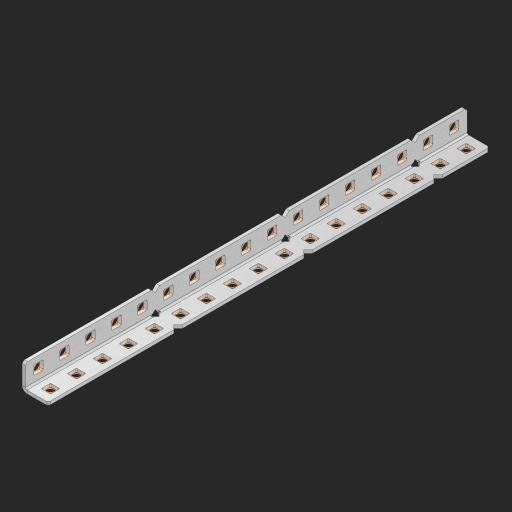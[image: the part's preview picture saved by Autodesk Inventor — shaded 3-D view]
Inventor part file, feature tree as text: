
AUTODESK INVENTOR PART (.ipt)
format: ipt  version: 2023 (Build 270158000, 158)  size: 751,616 bytes
history: native  units: in
note: dims shown in document units (in); Inventor stores cm internally (conversion verified against a paired STEP export)
features: other x40, extrude x35, sheet_metal_op x8, sketch x5, pattern_linear x1, mirror x1, chamfer x1
ambient origin geometry x8: Origin, YZ Plane, XZ Plane, XY Plane, X Axis, Y Axis, Z Axis, Center Point
bodies: Solid1 (feature_tree), Body (feature_tree)
feature tree (91):
  sheet_metal_op  "Flanges"
  sheet_metal_op  "Body Pattern"
  other  "Arc Length"
  pattern_linear  "Notch Pattern"  Spacing1=0.125in  [1 undecoded]
  other  "Diagonal Plane"
  mirror  "Everything Mirrored"
  chamfer  "End Chamfer"
  sketch  "Sketch1"  dims[d0=0.5in]
  other  "Plate1"
  sketch  "Sketch2"  dims[d1=8.5in]
  other  "Plate2"
  sheet_metal_op  "Bend1"
  sheet_metal_op  "Corner1"
  sketch  "Sketch8"  dims[d2=0.0625in]
  sketch  "Sketch9"  dims[d3=0.0625in]
  other  "Srf91"
  sheet_metal_op  "Body Pattern Sketch"
  other  "Srf92"
  sketch  "Sketch13"  dims[d4=0.0312in d5=0.125in d6=0.0625in d7=0.5in d8=90.0deg d9=0.0312in d10=0.25in d11=0.0625in d12=0.0625in d49=0.182in d50=0.02in d52=0.25in d53=0.0625in d54=0.0in d55=0.172in d56=1.0in d57=0.0in d85=0.1473in d86=0.1782in d89=0.0625in d90=0.0in d91=0.04in d92=0.0491in d95=2.5in d96=0.04in d97=0.25in d98=45.0deg d123=0.204in d126=0.0491in d127=0.1473in d128=0.08in d129=0.04in d130=2.5in d131=6.6929in d133=0.5in d134=0.3937in d136=1.0in]
  other  "Srf856"
  other  "Srf857"
  other  "Srf858"
  other  "Srf859"
  other  "Srf860"
  other  "Srf861"
  other  "Srf1275"
  other  "Srf1276"
  other  "Srf1278"
  other  "Srf1279"
  other  "Srf1280"
  other  "Srf1281"
  other  "Srf1282"
  other  "Srf1283"
  other  "Srf1383"
  other  "Srf1384"
  other  "Srf1385"
  other  "Srf1386"
  other  "Srf1387"
  other  "Srf1388"
  other  "Srf1389"
  other  "Srf1390"
  other  "Srf1391"
  other  "Srf1392"
  other  "Srf1475"
  other  "Srf1476"
  other  "Srf1477"
  other  "Srf1478"
  other  "Srf1479"
  other  "Srf1480"
  other  "Srf1481"
  other  "Srf1482"
  other  "Srf1483"
  other  "Srf1484"
  sheet_metal_op  "Body Stamp"
  sheet_metal_op  "Body Circle"
  sheet_metal_op  "Notch"
  extrude  "ExtrusionSrf92"  Depth=0.0625in
  extrude  "ExtrusionSrf856"  Depth=0.5in TaperAngle=90.0deg
  extrude  "ExtrusionSrf857"  Depth=0.25in
  extrude  "ExtrusionSrf858"  Depth=0.0625in
  extrude  "ExtrusionSrf859"  Depth=0.0625in
  extrude  "ExtrusionSrf860"  Depth=0.3937in
  extrude  "ExtrusionSrf861"  Depth=0.02in
  extrude  "ExtrusionSrf1275"  Depth=0.25in
  extrude  "ExtrusionSrf1276"  Depth=0.0625in
  extrude  "ExtrusionSrf1277"  TaperAngle=0.0deg  [1 undecoded]
  extrude  "ExtrusionSrf1278"  Depth=0.3937in
  extrude  "ExtrusionSrf1279"  Depth=0.3937in TaperAngle=0.0deg
  extrude  "ExtrusionSrf1280"  Depth=0.3937in
  extrude  "ExtrusionSrf1281"  Depth=0.3937in
  extrude  "ExtrusionSrf1282"  Depth=0.0625in
  extrude  "ExtrusionSrf1383"  Depth=0.3937in TaperAngle=0.0deg
  extrude  "ExtrusionSrf1384"  Depth=0.3937in
  extrude  "ExtrusionSrf1385"  Depth=0.25in TaperAngle=45.0deg
  extrude  "ExtrusionSrf1386"  Depth=0.3937in
  extrude  "ExtrusionSrf1387"  Depth=0.3937in
  extrude  "ExtrusionSrf1388"  Depth=0.3937in
  extrude  "ExtrusionSrf1389"  Depth=0.3937in
  extrude  "ExtrusionSrf1390"  Depth=0.3937in
  extrude  "ExtrusionSrf1391"  Depth=0.3937in
  extrude  "ExtrusionSrf1392"  Depth=0.3937in
  extrude  "ExtrusionSrf1475"  Depth=0.5in
  extrude  "ExtrusionSrf1476"  [1 undecoded]
  extrude  "ExtrusionSrf1477"  [1 undecoded]
  extrude  "ExtrusionSrf1478"  [1 undecoded]
  extrude  "ExtrusionSrf1479"  [1 undecoded]
  extrude  "ExtrusionSrf1480"  [1 undecoded]
  extrude  "ExtrusionSrf1481"  [1 undecoded]
  extrude  "ExtrusionSrf1482"  [1 undecoded]
  extrude  "ExtrusionSrf1483"  [1 undecoded]
  extrude  "ExtrusionSrf1484"  [1 undecoded]
note: 11 required parameter values undecoded (feature->parameter linkage not recoverable at this tier; creation-order binding heuristic only, values carry confidence <= 0.55)
